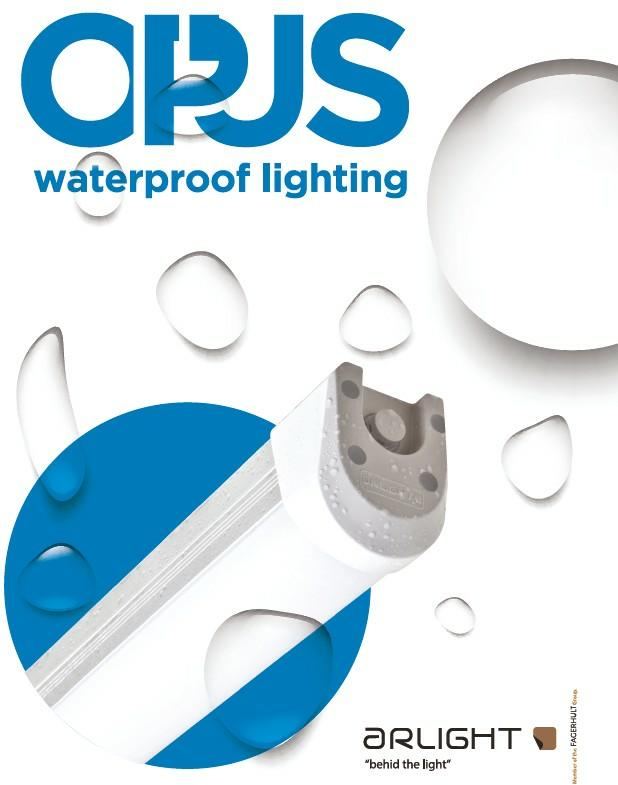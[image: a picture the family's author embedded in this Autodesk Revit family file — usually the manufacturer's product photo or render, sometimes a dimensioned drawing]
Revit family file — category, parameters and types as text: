
# Revit family: E 0600 PUS
name_source: partatom
category: Lighting Fixtures
revit_build: Autodesk Revit 2017 (Build: 20160225_1515(x64)
units: mm (PartAtom-declared; Revit-internal decimal feet)

## family parameters
Cut with Voids When Loaded = No
Host = Face
Light Source = Yes
Part Type = Normal
Room Calculation Point = No
Round Connector Dimension = Use Diameter
Shared = No

## types (8) — shared parameters
Color Filter = 16777215
Default Elevation = 1219 mm
Description = Double Connector
Dimming Lamp Color Temperature Shift = <None>
Emit Shape Visible in Rendering = No
Emit from Rectangle Length = 562 mm  [stored 1.84383 ft]
Emit from Rectangle Width = 55 mm  [stored 0.180446 ft]
Lamp = LED
Manufacturer = ARLIGHT AYDINLATMA
Model = E 0600 PUS (CK)
Photometric Web File = E 1500 PUS-59W-4K(SK).IES
Tilt Angle = -90.00°
Type Comments = Waterproof Lighting
Type Image = OPUS.jpg
URL = http://www.arlight.net

## per-type parameters (varying)
| type | Apparent Load | Wattage Comments |
| EPUS.600.19.40.TK | 19 VA | 19W |
| EPUS.600.26.40.TK | 26 VA | 26W |
| EPUS.600.19.40.CK | 19 VA | 19W |
| EPUS.600.26.40.CK | 26 VA | 26W |
| EPUS.600.19.40.TR | 19 VA | 19W |
| EPUS.600.26.40.TR | 26 VA | 26W |
| EPUS.600.19.40.CR | 19 VA | 19W |
| EPUS600.26.40.CR | 19 VA | 26W |

note: [stored X ft] marks values corroborated as IEEE doubles in the binary element streams (Revit-internal decimal feet)

## geometry (parser evidence)
native form markers: Sweep x3
no freeform markers — native parametric forms only
